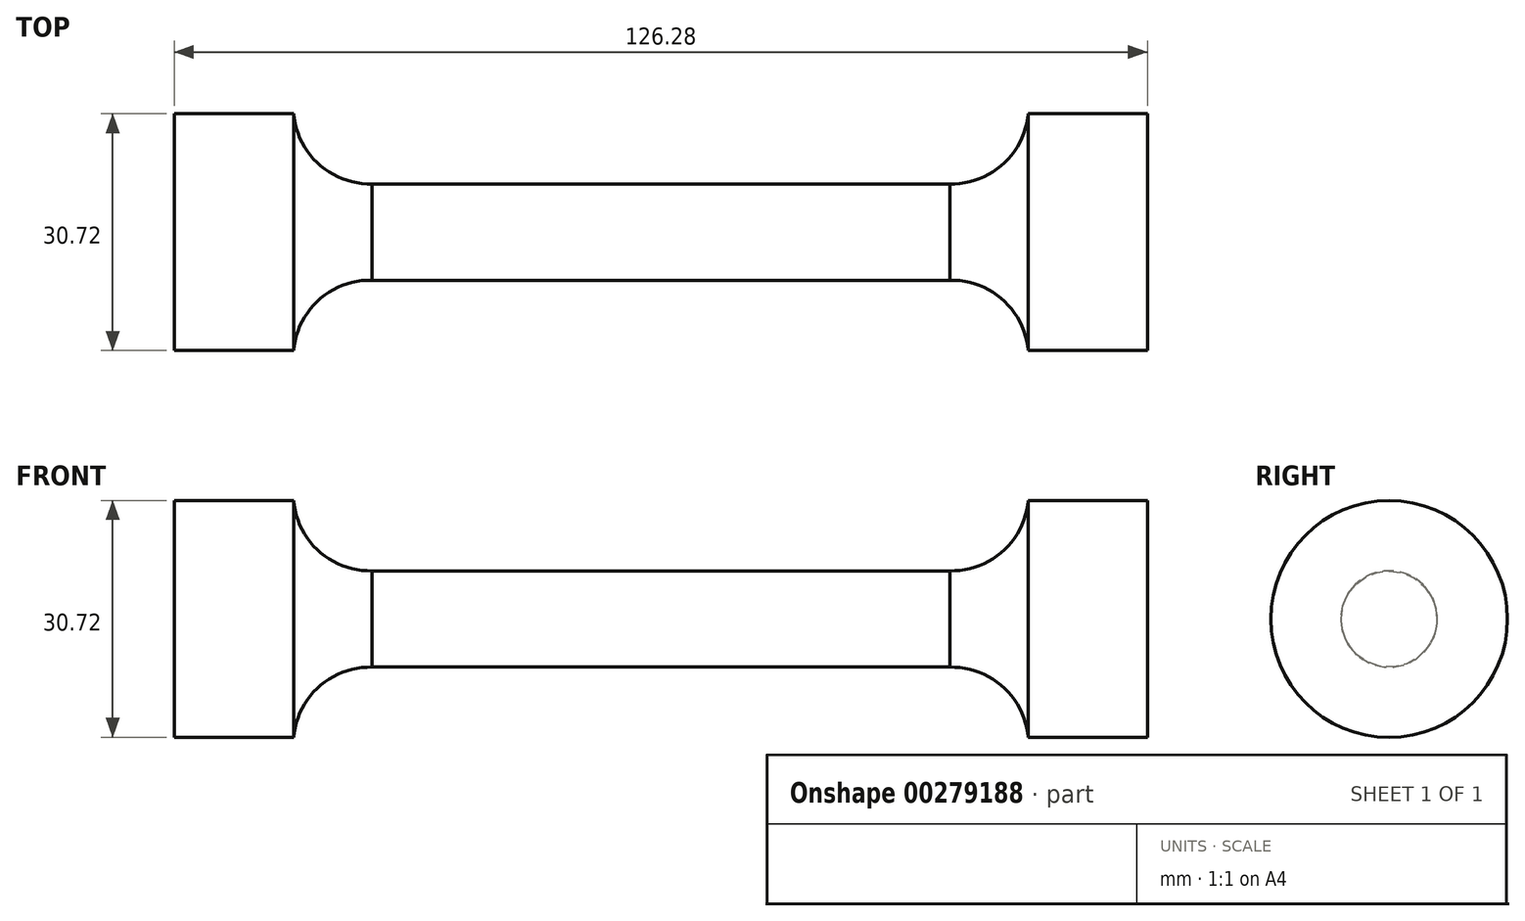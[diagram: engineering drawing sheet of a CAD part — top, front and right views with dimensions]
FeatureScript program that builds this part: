
annotation { "Feature Type Name" : "Feature", "Feature Type Description" : "" }
export const myFeature = defineFeature(function(context is Context, id is Id, definition is map)
    precondition{}
    {
        {
            var Q0;
            Q0=qCreatedBy(makeId("Front.planeOp"),FACE);
            var sketch = newSketch(context, id + "F0", { "sketchPlane" : qUnion([Q0])});
            skLineSegment(sketch, "E0", {"start": v(0, 6.25) * mm, "end": v(37.5, 6.25) * mm});
            skArc(sketch, "E1", {"start": v(37.5, 6.25) * mm, "mid": v(44.38, 8.8) * mm, "end": v(47.67, 15.36) * mm});
            skLineSegment(sketch, "E2", {"start": v(47.67, 15.36) * mm, "end": v(63.14, 15.36) * mm});
            skLineSegment(sketch, "E3", {"start": v(63.14, 15.36) * mm, "end": v(63.14, 0) * mm});
            skLineSegment(sketch, "E4.MirrorCS", {"start": v(0, 6.25) * mm, "end": v(-37.5, 6.25) * mm});
            skArc(sketch, "E5.MirrorCS", {"start": v(-37.5, 6.25) * mm, "mid": v(-44.38, 8.8) * mm, "end": v(-47.67, 15.36) * mm});
            skLineSegment(sketch, "E6.MirrorCS", {"start": v(-63.14, 15.36) * mm, "end": v(-63.14, 0) * mm});
            skLineSegment(sketch, "E7.MirrorCS", {"start": v(-47.67, 15.36) * mm, "end": v(-63.14, 15.36) * mm});
            skLineSegment(sketch, "E8", {"start": v(-63.14, 0) * mm, "end": v(63.14, 0) * mm});
            skSolve(sketch);
        }
        {
            var Q0;
            Q0 = qSketchRegion(id + "F0", true);
            var Q1;
            Q1=sQuery(id+"F0.wireOp",EDGE,"E8");
            revolve(context, id + "F1", {"entities" : qUnion([Q0]), "axis" : qUnion([Q1]), "revolveType" : RevolveType.FULL});
        }
    });
